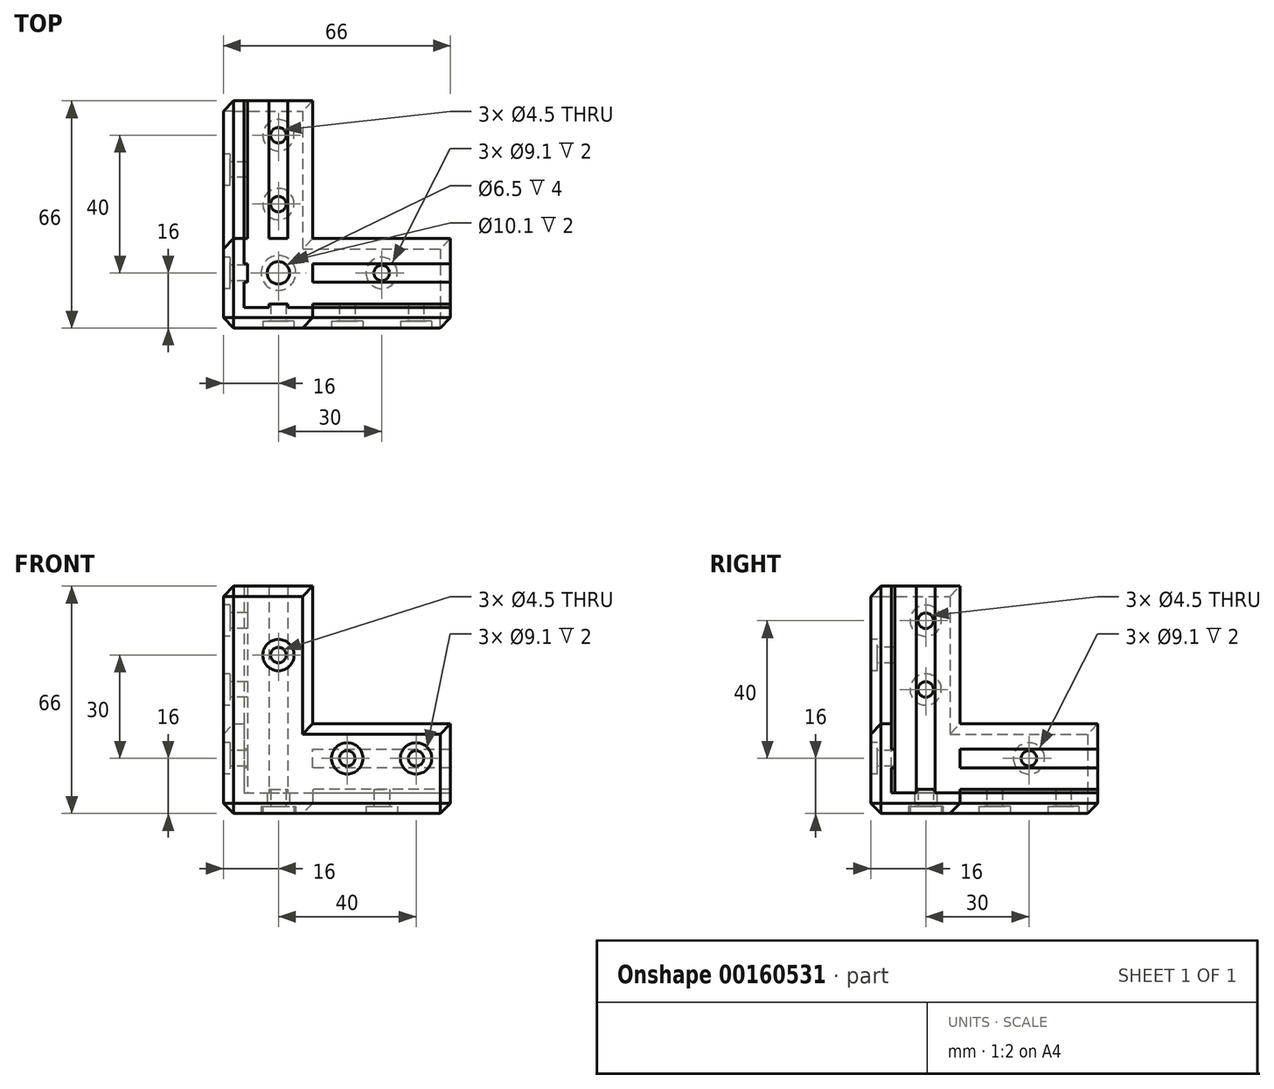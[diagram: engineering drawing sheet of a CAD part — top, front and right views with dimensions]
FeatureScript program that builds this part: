
annotation { "Feature Type Name" : "Feature", "Feature Type Description" : "" }
export const myFeature = defineFeature(function(context is Context, id is Id, definition is map)
    precondition{}
    {
        {
            var Q0;
            Q0=qCreatedBy(makeId("Top.planeOp"),FACE);
            var sketch = newSketch(context, id + "F0", { "sketchPlane" : qUnion([Q0])});
            skLineSegment(sketch, "E0", {"start": v(0, 0) * mm, "end": v(0, 66) * mm});
            skLineSegment(sketch, "E1", {"start": v(0, 66) * mm, "end": v(26, 66) * mm});
            skLineSegment(sketch, "E2", {"start": v(26, 66) * mm, "end": v(26, 26) * mm});
            skLineSegment(sketch, "E3", {"start": v(26, 26) * mm, "end": v(66, 26) * mm});
            skLineSegment(sketch, "E4", {"start": v(66, 26) * mm, "end": v(66, 0) * mm});
            skLineSegment(sketch, "E5", {"start": v(66, 0) * mm, "end": v(0, 0) * mm});
            skLineSegment(sketch, "E6", {"start": v(66, 6) * mm, "end": v(6, 6) * mm, "construction": true});
            skLineSegment(sketch, "E7", {"start": v(6, 6) * mm, "end": v(6, 66) * mm, "construction": true});
            skSolve(sketch);
        }
        {
            var Q0;
            Q0 = qSketchRegion(id + "F0", true);
            extrude(context, id + "F1", {"entities" : qUnion([Q0]), "depth" : 6 * mm});
        }
        {
            var Q0;
            Q0=makeQuery(id+"F1.opExtrude","CAP_FACE",FACE,{"disambiguationData":[OSD([sQuery(id+"F0.wireOp",EDGE,"E0"),sQuery(id+"F0.wireOp",EDGE,"E1"),sQuery(id+"F0.wireOp",EDGE,"E2"),sQuery(id+"F0.wireOp",EDGE,"E3"),sQuery(id+"F0.wireOp",EDGE,"E4"),sQuery(id+"F0.wireOp",EDGE,"E5")])],"isStart":false});
            var sketch = newSketch(context, id + "F2", { "sketchPlane" : qUnion([Q0])});
            skLineSegment(sketch, "E8", {"start": v(0, 66) * mm, "end": v(6, 66) * mm});
            skLineSegment(sketch, "E9", {"start": v(6, 66) * mm, "end": v(6, 6) * mm});
            skLineSegment(sketch, "E10", {"start": v(6, 6) * mm, "end": v(66, 6) * mm});
            skLineSegment(sketch, "E11", {"start": v(66, 6) * mm, "end": v(66, 0) * mm});
            skLineSegment(sketch, "E12", {"start": v(66, 0) * mm, "end": v(0, 0) * mm});
            skLineSegment(sketch, "E13", {"start": v(0, 0) * mm, "end": v(0, 66) * mm});
            skSolve(sketch);
        }
        {
            var Q0;
            Q0=makeQuery(id+"F2.imprint","IMPRINT",FACE,{"disambiguationData":[TD([[makeQuery(id+"F2.imprint","IMPRINT",EDGE,{"derivedFrom":sQuery(id+"F2.wireOp",EDGE,"E8")}),-1.0]])]});
            extrude(context, id + "F3", {"entities" : qUnion([Q0]), "operationType" : NewBodyOperationType.ADD, "depth" : 20 * mm});
        }
        {
            var Q0;
            Q0=makeQuery(id+"F3.opExtrude","CAP_FACE",FACE,{"disambiguationData":[OSD([sQuery(id+"F2.wireOp",EDGE,"E8"),sQuery(id+"F2.wireOp",EDGE,"E9"),sQuery(id+"F2.wireOp",EDGE,"E10"),sQuery(id+"F2.wireOp",EDGE,"E11"),sQuery(id+"F2.wireOp",EDGE,"E12"),sQuery(id+"F2.wireOp",EDGE,"E13")])],"isStart":false});
            var sketch = newSketch(context, id + "F4", { "sketchPlane" : qUnion([Q0])});
            skLineSegment(sketch, "E14", {"start": v(6, 26) * mm, "end": v(0, 26) * mm});
            skLineSegment(sketch, "E15", {"start": v(0, 26) * mm, "end": v(0, 0) * mm});
            skLineSegment(sketch, "E16", {"start": v(0, 0) * mm, "end": v(26, 0) * mm});
            skLineSegment(sketch, "E17", {"start": v(26, 0) * mm, "end": v(26, 6) * mm});
            skLineSegment(sketch, "E18", {"start": v(26, 6) * mm, "end": v(6, 6) * mm});
            skLineSegment(sketch, "E19", {"start": v(6, 6) * mm, "end": v(6, 26) * mm});
            skSolve(sketch);
        }
        {
            var Q0;
            Q0 = qSketchRegion(id + "F4", true);
            extrude(context, id + "F5", {"entities" : qUnion([Q0]), "operationType" : NewBodyOperationType.ADD, "depth" : 40 * mm});
        }
        {
            var Q0;
            Q0=makeQuery(id+"F1.opExtrude","CAP_FACE",FACE,{"disambiguationData":[OSD([sQuery(id+"F0.wireOp",EDGE,"E0"),sQuery(id+"F0.wireOp",EDGE,"E1"),sQuery(id+"F0.wireOp",EDGE,"E2"),sQuery(id+"F0.wireOp",EDGE,"E3"),sQuery(id+"F0.wireOp",EDGE,"E4"),sQuery(id+"F0.wireOp",EDGE,"E5")])],"isStart":false});
            var sketch = newSketch(context, id + "F6", { "sketchPlane" : qUnion([Q0])});
            skLineSegment(sketch, "E20", {"start": v(66, 16) * mm, "end": v(6, 16) * mm, "construction": true});
            skLineSegment(sketch, "E21", {"start": v(16, 66) * mm, "end": v(16, 6) * mm, "construction": true});
            skLineSegment(sketch, "E22", {"start": v(16, 6) * mm, "end": v(18.71, 6) * mm});
            skLineSegment(sketch, "E23", {"start": v(18.71, 6) * mm, "end": v(18.71, 7) * mm});
            skLineSegment(sketch, "E24", {"start": v(18.71, 7) * mm, "end": v(13.3, 7) * mm});
            skLineSegment(sketch, "E25", {"start": v(13.3, 7) * mm, "end": v(13.3, 6) * mm});
            skLineSegment(sketch, "E26", {"start": v(13.3, 6) * mm, "end": v(16, 6) * mm});
            skLineSegment(sketch, "E27", {"start": v(6, 16) * mm, "end": v(6, 18.7) * mm});
            skLineSegment(sketch, "E28", {"start": v(6, 18.7) * mm, "end": v(7, 18.7) * mm});
            skLineSegment(sketch, "E29", {"start": v(7, 18.7) * mm, "end": v(7, 13.29) * mm});
            skLineSegment(sketch, "E30", {"start": v(7, 13.29) * mm, "end": v(6, 13.29) * mm});
            skLineSegment(sketch, "E31", {"start": v(6, 13.29) * mm, "end": v(6, 16) * mm});
            skSolve(sketch);
        }
        {
            var Q0;
            Q0 = qSketchRegion(id + "F6", true);
            extrude(context, id + "F7", {"entities" : qUnion([Q0]), "operationType" : NewBodyOperationType.ADD, "depth" : 60 * mm});
        }
        {
            var Q0;
            Q0=makeQuery(id+"F1.opExtrude","CAP_FACE",FACE,{"disambiguationData":[OSD([sQuery(id+"F0.wireOp",EDGE,"E0"),sQuery(id+"F0.wireOp",EDGE,"E1"),sQuery(id+"F0.wireOp",EDGE,"E2"),sQuery(id+"F0.wireOp",EDGE,"E3"),sQuery(id+"F0.wireOp",EDGE,"E4"),sQuery(id+"F0.wireOp",EDGE,"E5")])],"isStart":false});
            var sketch = newSketch(context, id + "F8", { "sketchPlane" : qUnion([Q0])});
            skLineSegment(sketch, "E32", {"start": v(66, 16) * mm, "end": v(7, 16) * mm, "construction": true});
            skLineSegment(sketch, "E33", {"start": v(66, 16) * mm, "end": v(66, 18.7) * mm});
            skLineSegment(sketch, "E34", {"start": v(66, 18.7) * mm, "end": v(26, 18.7) * mm});
            skLineSegment(sketch, "E35", {"start": v(26, 18.7) * mm, "end": v(26, 13.29) * mm});
            skLineSegment(sketch, "E36", {"start": v(26, 13.29) * mm, "end": v(66, 13.29) * mm});
            skLineSegment(sketch, "E37", {"start": v(66, 13.29) * mm, "end": v(66, 16) * mm});
            skLineSegment(sketch, "E38", {"start": v(16, 66) * mm, "end": v(16, 7) * mm, "construction": true});
            skLineSegment(sketch, "E39", {"start": v(16, 66) * mm, "end": v(13.3, 66) * mm});
            skLineSegment(sketch, "E40", {"start": v(13.3, 66) * mm, "end": v(13.3, 26) * mm});
            skLineSegment(sketch, "E41", {"start": v(13.3, 26) * mm, "end": v(18.7, 26) * mm});
            skLineSegment(sketch, "E42", {"start": v(18.7, 26) * mm, "end": v(18.7, 66) * mm});
            skLineSegment(sketch, "E43", {"start": v(18.7, 66) * mm, "end": v(16, 66) * mm});
            skSolve(sketch);
        }
        {
            var Q0;
            Q0 = qSketchRegion(id + "F8", true);
            extrude(context, id + "F9", {"entities" : qUnion([Q0]), "operationType" : NewBodyOperationType.ADD, "flatOperationType" : FlatOperationType.REMOVE, "offsetDistance" : 25 * mm, "depth" : 1 * mm, "domain" : OperationDomain.MODEL});
        }
        {
            var Q0;
            {var subQ1=sQuery(id+"F2.wireOp",EDGE,"E10");var subQ2=sQuery(id+"F0.wireOp",EDGE,"E4");var subQ3=sQuery(id+"F4.wireOp",EDGE,"E18");Q0=makeQuery(id+"F7.boolean.opBoolean","SPLIT",FACE,{"disambiguationData":[TD([makeQuery(id+"F1.opExtrude","SWEPT_FACE",FACE,{"disambiguationData":[OSD([subQ2])]})])],"derivedFrom":makeQuery(id+"F5.boolean.opBoolean","MERGE",FACE,{"derivedFrom":[makeQuery(id+"F3.opExtrude","SWEPT_FACE",FACE,{"disambiguationData":[OSD([subQ1])]}),makeQuery(id+"F5.opExtrude","SWEPT_FACE",FACE,{"disambiguationData":[OSD([subQ3])]})]})});}
            var sketch = newSketch(context, id + "F10", { "sketchPlane" : qUnion([Q0])});
            skLineSegment(sketch, "E44", {"start": v(-66, 16) * mm, "end": v(-26, 16) * mm, "construction": true});
            skLineSegment(sketch, "E45", {"start": v(-66, 16) * mm, "end": v(-66, 13.3) * mm});
            skLineSegment(sketch, "E46", {"start": v(-66, 13.3) * mm, "end": v(-26, 13.3) * mm});
            skLineSegment(sketch, "E47", {"start": v(-26, 13.3) * mm, "end": v(-26, 16) * mm});
            skLineSegment(sketch, "E48", {"start": v(-26, 18.71) * mm, "end": v(-66, 18.71) * mm});
            skLineSegment(sketch, "E49", {"start": v(-66, 18.71) * mm, "end": v(-66, 16) * mm});
            skLineSegment(sketch, "E50", {"start": v(-26, 18.71) * mm, "end": v(-26, 16) * mm});
            skSolve(sketch);
        }
        {
            var Q0;
            Q0 = qSketchRegion(id + "F10", true);
            extrude(context, id + "F11", {"entities" : qUnion([Q0]), "operationType" : NewBodyOperationType.ADD, "flatOperationType" : FlatOperationType.REMOVE, "offsetDistance" : 25 * mm, "depth" : 1 * mm, "domain" : OperationDomain.MODEL});
        }
        {
            var Q0;
            {var subQ0=sQuery(id+"F2.wireOp",EDGE,"E9");var subQ3=sQuery(id+"F0.wireOp",EDGE,"E1");var subQ5=sQuery(id+"F4.wireOp",EDGE,"E19");Q0=makeQuery(id+"F7.boolean.opBoolean","SPLIT",FACE,{"disambiguationData":[TD([makeQuery(id+"F1.opExtrude","SWEPT_FACE",FACE,{"disambiguationData":[OSD([subQ3])]})])],"derivedFrom":makeQuery(id+"F5.boolean.opBoolean","MERGE",FACE,{"derivedFrom":[makeQuery(id+"F3.opExtrude","SWEPT_FACE",FACE,{"disambiguationData":[OSD([subQ0])]}),makeQuery(id+"F5.opExtrude","SWEPT_FACE",FACE,{"disambiguationData":[OSD([subQ5])]})]})});}
            var sketch = newSketch(context, id + "F12", { "sketchPlane" : qUnion([Q0])});
            skLineSegment(sketch, "E51", {"start": v(66, 16) * mm, "end": v(26, 16) * mm, "construction": true});
            skLineSegment(sketch, "E52", {"start": v(66, 16) * mm, "end": v(66, 18.71) * mm});
            skLineSegment(sketch, "E53", {"start": v(66, 18.71) * mm, "end": v(26, 18.7) * mm});
            skLineSegment(sketch, "E54", {"start": v(26, 18.7) * mm, "end": v(26, 13.29) * mm});
            skLineSegment(sketch, "E55", {"start": v(26, 13.29) * mm, "end": v(66, 13.29) * mm});
            skLineSegment(sketch, "E56", {"start": v(66, 16) * mm, "end": v(66, 13.29) * mm});
            skSolve(sketch);
        }
        {
            var Q0;
            Q0 = qSketchRegion(id + "F12", true);
            extrude(context, id + "F13", {"entities" : qUnion([Q0]), "operationType" : NewBodyOperationType.ADD, "flatOperationType" : FlatOperationType.REMOVE, "offsetDistance" : 25 * mm, "depth" : 1 * mm, "domain" : OperationDomain.MODEL});
        }
        {
            var Q0;
            Q0=makeQuery(id+"F5.boolean.opBoolean","MERGE",FACE,{"derivedFrom":[makeQuery(id+"F3.boolean.opBoolean","MERGE",FACE,{"derivedFrom":[makeQuery(id+"F1.opExtrude","SWEPT_FACE",FACE,{"disambiguationData":[OSD([sQuery(id+"F0.wireOp",EDGE,"E5")])]}),makeQuery(id+"F3.opExtrude","SWEPT_FACE",FACE,{"disambiguationData":[OSD([sQuery(id+"F2.wireOp",EDGE,"E12")])]})]}),makeQuery(id+"F5.opExtrude","SWEPT_FACE",FACE,{"disambiguationData":[OSD([sQuery(id+"F4.wireOp",EDGE,"E16")])]})]});
            var sketch = newSketch(context, id + "F14", { "sketchPlane" : qUnion([Q0])});
            skLineSegment(sketch, "E57", {"start": v(6, 66) * mm, "end": v(6, 6) * mm, "construction": true});
            skLineSegment(sketch, "E58", {"start": v(6, 6) * mm, "end": v(66, 6) * mm, "construction": true});
            skCircle(sketch, "E59", {"center": v(56, 16) * mm, "radius": 2.25 * mm});
            skCircle(sketch, "E60", {"center": v(36, 16) * mm, "radius": 2.25 * mm});
            skCircle(sketch, "E61", {"center": v(16, 46) * mm, "radius": 2.25 * mm});
            skLineSegment(sketch, "E62", {"start": v(26, 26) * mm, "end": v(6, 26) * mm, "construction": true});
            skLineSegment(sketch, "E63", {"start": v(26, 26) * mm, "end": v(26, 6) * mm, "construction": true});
            skSolve(sketch);
        }
        {
            var Q0;
            Q0=makeQuery(id+"F14.imprint","IMPRINT",FACE,{"disambiguationData":[TD([[makeQuery(id+"F14.imprint","IMPRINT",EDGE,{"derivedFrom":sQuery(id+"F14.wireOp",EDGE,"E59")}),1.0]])]});
            var Q1;
            Q1=makeQuery(id+"F14.imprint","IMPRINT",FACE,{"disambiguationData":[TD([[makeQuery(id+"F14.imprint","IMPRINT",EDGE,{"derivedFrom":sQuery(id+"F14.wireOp",EDGE,"E61")}),1.0]])]});
            var Q2;
            Q2=makeQuery(id+"F14.imprint","IMPRINT",FACE,{"disambiguationData":[TD([[makeQuery(id+"F14.imprint","IMPRINT",EDGE,{"derivedFrom":sQuery(id+"F14.wireOp",EDGE,"E60")}),1.0]])]});
            extrude(context, id + "F15", {"entities" : qUnion([Q0, Q1, Q2]), "operationType" : NewBodyOperationType.REMOVE, "endBound" : BoundingType.UP_TO_NEXT, "oppositeDirection" : true, "depth" : 25 * mm});
        }
        {
            var Q0;
            Q0=makeQuery(id+"F5.boolean.opBoolean","MERGE",FACE,{"derivedFrom":[makeQuery(id+"F3.boolean.opBoolean","MERGE",FACE,{"derivedFrom":[makeQuery(id+"F1.opExtrude","SWEPT_FACE",FACE,{"disambiguationData":[OSD([sQuery(id+"F0.wireOp",EDGE,"E0")])]}),makeQuery(id+"F3.opExtrude","SWEPT_FACE",FACE,{"disambiguationData":[OSD([sQuery(id+"F2.wireOp",EDGE,"E13")])]})]}),makeQuery(id+"F5.opExtrude","SWEPT_FACE",FACE,{"disambiguationData":[OSD([sQuery(id+"F4.wireOp",EDGE,"E15")])]})]});
            var sketch = newSketch(context, id + "F16", { "sketchPlane" : qUnion([Q0])});
            skLineSegment(sketch, "E64", {"start": v(-6, 66) * mm, "end": v(-6, 6) * mm, "construction": true});
            skLineSegment(sketch, "E65", {"start": v(-6, 6) * mm, "end": v(-66, 6) * mm, "construction": true});
            skCircle(sketch, "E66", {"center": v(-16, 56) * mm, "radius": 2.25 * mm});
            skCircle(sketch, "E67", {"center": v(-46, 16) * mm, "radius": 2.25 * mm});
            skCircle(sketch, "E68", {"center": v(-16, 36) * mm, "radius": 2.25 * mm});
            skSolve(sketch);
        }
        {
            var Q0;
            Q0 = qSketchRegion(id + "F16", true);
            extrude(context, id + "F17", {"entities" : qUnion([Q0]), "operationType" : NewBodyOperationType.REMOVE, "endBound" : BoundingType.UP_TO_NEXT, "oppositeDirection" : true, "depth" : 25 * mm});
        }
        {
            var Q0;
            Q0=makeQuery(id+"F1.opExtrude","CAP_FACE",FACE,{"disambiguationData":[OSD([sQuery(id+"F0.wireOp",EDGE,"E0"),sQuery(id+"F0.wireOp",EDGE,"E1"),sQuery(id+"F0.wireOp",EDGE,"E2"),sQuery(id+"F0.wireOp",EDGE,"E3"),sQuery(id+"F0.wireOp",EDGE,"E4"),sQuery(id+"F0.wireOp",EDGE,"E5")])],"isStart":true});
            var sketch = newSketch(context, id + "F18", { "sketchPlane" : qUnion([Q0])});
            skLineSegment(sketch, "E69", {"start": v(66, -6) * mm, "end": v(6, -6) * mm, "construction": true});
            skLineSegment(sketch, "E70", {"start": v(6, -6) * mm, "end": v(6, -66) * mm, "construction": true});
            skCircle(sketch, "E71", {"center": v(16, -16) * mm, "radius": 3.25 * mm});
            skCircle(sketch, "E72", {"center": v(46, -16) * mm, "radius": 2.25 * mm});
            skCircle(sketch, "E73", {"center": v(16, -56) * mm, "radius": 2.25 * mm});
            skCircle(sketch, "E74", {"center": v(16, -36) * mm, "radius": 2.25 * mm});
            skSolve(sketch);
        }
        {
            var Q0;
            Q0 = qSketchRegion(id + "F18", true);
            extrude(context, id + "F19", {"entities" : qUnion([Q0]), "operationType" : NewBodyOperationType.REMOVE, "endBound" : BoundingType.UP_TO_NEXT, "oppositeDirection" : true, "depth" : 25 * mm});
        }
        {
            var Q0;
            Q0=makeQuery(id+"F5.boolean.opBoolean","MERGE",FACE,{"derivedFrom":[makeQuery(id+"F3.boolean.opBoolean","MERGE",FACE,{"derivedFrom":[makeQuery(id+"F1.opExtrude","SWEPT_FACE",FACE,{"disambiguationData":[OSD([sQuery(id+"F0.wireOp",EDGE,"E5")])]}),makeQuery(id+"F3.opExtrude","SWEPT_FACE",FACE,{"disambiguationData":[OSD([sQuery(id+"F2.wireOp",EDGE,"E12")])]})]}),makeQuery(id+"F5.opExtrude","SWEPT_FACE",FACE,{"disambiguationData":[OSD([sQuery(id+"F4.wireOp",EDGE,"E16")])]})]});
            var sketch = newSketch(context, id + "F20", { "sketchPlane" : qUnion([Q0])});
            skCircle(sketch, "E75", {"center": v(16, 46) * mm, "radius": 4.55 * mm});
            skCircle(sketch, "E76", {"center": v(36, 16) * mm, "radius": 4.55 * mm});
            skCircle(sketch, "E77", {"center": v(56, 16) * mm, "radius": 4.55 * mm});
            skSolve(sketch);
        }
        {
            var Q0;
            Q0 = qSketchRegion(id + "F20", true);
            extrude(context, id + "F21", {"entities" : qUnion([Q0]), "operationType" : NewBodyOperationType.REMOVE, "oppositeDirection" : true, "depth" : 2 * mm});
        }
        {
            var Q0;
            Q0=makeQuery(id+"F5.boolean.opBoolean","MERGE",FACE,{"derivedFrom":[makeQuery(id+"F3.boolean.opBoolean","MERGE",FACE,{"derivedFrom":[makeQuery(id+"F1.opExtrude","SWEPT_FACE",FACE,{"disambiguationData":[OSD([sQuery(id+"F0.wireOp",EDGE,"E0")])]}),makeQuery(id+"F3.opExtrude","SWEPT_FACE",FACE,{"disambiguationData":[OSD([sQuery(id+"F2.wireOp",EDGE,"E13")])]})]}),makeQuery(id+"F5.opExtrude","SWEPT_FACE",FACE,{"disambiguationData":[OSD([sQuery(id+"F4.wireOp",EDGE,"E15")])]})]});
            var sketch = newSketch(context, id + "F22", { "sketchPlane" : qUnion([Q0])});
            skCircle(sketch, "E78", {"center": v(-16, 56) * mm, "radius": 4.55 * mm});
            skCircle(sketch, "E79", {"center": v(-46, 16) * mm, "radius": 4.55 * mm});
            skCircle(sketch, "E80", {"center": v(-16, 36) * mm, "radius": 4.55 * mm});
            skSolve(sketch);
        }
        {
            var Q0;
            Q0 = qSketchRegion(id + "F22", true);
            extrude(context, id + "F23", {"entities" : qUnion([Q0]), "operationType" : NewBodyOperationType.REMOVE, "oppositeDirection" : true, "depth" : 2 * mm});
        }
        {
            var Q0;
            Q0=makeQuery(id+"F1.opExtrude","CAP_FACE",FACE,{"disambiguationData":[OSD([sQuery(id+"F0.wireOp",EDGE,"E0"),sQuery(id+"F0.wireOp",EDGE,"E1"),sQuery(id+"F0.wireOp",EDGE,"E2"),sQuery(id+"F0.wireOp",EDGE,"E3"),sQuery(id+"F0.wireOp",EDGE,"E4"),sQuery(id+"F0.wireOp",EDGE,"E5")])],"isStart":true});
            var sketch = newSketch(context, id + "F24", { "sketchPlane" : qUnion([Q0])});
            skCircle(sketch, "E81", {"center": v(16, -56) * mm, "radius": 4.55 * mm});
            skCircle(sketch, "E82", {"center": v(16, -16) * mm, "radius": 5.05 * mm});
            skCircle(sketch, "E83", {"center": v(46, -16) * mm, "radius": 4.55 * mm});
            skCircle(sketch, "E84", {"center": v(16, -36) * mm, "radius": 4.55 * mm});
            skSolve(sketch);
        }
        {
            var Q0;
            Q0 = qSketchRegion(id + "F24", true);
            extrude(context, id + "F25", {"entities" : qUnion([Q0]), "operationType" : NewBodyOperationType.REMOVE, "oppositeDirection" : true, "depth" : 2 * mm});
        }
        {
            var Q0;
            Q0=makeQuery(id+"F1.opExtrude","CAP_EDGE",EDGE,{"disambiguationData":[OSD([sQuery(id+"F0.wireOp",EDGE,"E5")])],"isStart":true});
            var Q1;
            Q1=makeQuery(id+"F1.opExtrude","CAP_EDGE",EDGE,{"disambiguationData":[OSD([sQuery(id+"F0.wireOp",EDGE,"E0")])],"isStart":true});
            var Q2;
            Q2=makeQuery(id+"F5.boolean.opBoolean","MERGE",EDGE,{"derivedFrom":[makeQuery(id+"F3.boolean.opBoolean","MERGE",EDGE,{"derivedFrom":[makeQuery(id+"F1.opExtrude","SWEPT_EDGE",EDGE,{"disambiguationData":[OSD([sQuery(id+"F0.wireOp",EDGE,"E0"),sQuery(id+"F0.wireOp",EDGE,"E5")])]}),makeQuery(id+"F3.opExtrude","SWEPT_EDGE",EDGE,{"disambiguationData":[OSD([sQuery(id+"F2.wireOp",EDGE,"E12"),sQuery(id+"F2.wireOp",EDGE,"E13")])]})]}),makeQuery(id+"F5.opExtrude","SWEPT_EDGE",EDGE,{"disambiguationData":[OSD([sQuery(id+"F4.wireOp",EDGE,"E15"),sQuery(id+"F4.wireOp",EDGE,"E16")])]})]});
            var Q3;
            Q3=makeQuery(id+"F5.opExtrude","SWEPT_EDGE",EDGE,{"disambiguationData":[OSD([sQuery(id+"F2.wireOp",EDGE,"E13"),sQuery(id+"F4.wireOp",EDGE,"E14"),sQuery(id+"F4.wireOp",EDGE,"E15")])]});
            var Q4;
            Q4=makeQuery(id+"F3.opExtrude","CAP_EDGE",EDGE,{"disambiguationData":[OSD([sQuery(id+"F2.wireOp",EDGE,"E13")])],"isStart":false});
            var Q5;
            Q5=makeQuery(id+"F5.opExtrude","SWEPT_EDGE",EDGE,{"disambiguationData":[OSD([sQuery(id+"F2.wireOp",EDGE,"E12"),sQuery(id+"F4.wireOp",EDGE,"E16"),sQuery(id+"F4.wireOp",EDGE,"E17")])]});
            var Q6;
            Q6=makeQuery(id+"F3.opExtrude","CAP_EDGE",EDGE,{"disambiguationData":[OSD([sQuery(id+"F2.wireOp",EDGE,"E12")])],"isStart":false});
            var Q7;
            Q7=makeQuery(id+"F5.opExtrude","CAP_EDGE",EDGE,{"disambiguationData":[OSD([sQuery(id+"F4.wireOp",EDGE,"E15")])],"isStart":false});
            var Q8;
            Q8=makeQuery(id+"F5.opExtrude","CAP_EDGE",EDGE,{"disambiguationData":[OSD([sQuery(id+"F4.wireOp",EDGE,"E16")])],"isStart":false});
            var Q9;
            Q9=makeQuery(id+"F3.boolean.opBoolean","MERGE",EDGE,{"derivedFrom":[makeQuery(id+"F1.opExtrude","SWEPT_EDGE",EDGE,{"disambiguationData":[OSD([sQuery(id+"F0.wireOp",EDGE,"E0"),sQuery(id+"F0.wireOp",EDGE,"E1")])]}),makeQuery(id+"F3.opExtrude","SWEPT_EDGE",EDGE,{"disambiguationData":[OSD([sQuery(id+"F2.wireOp",EDGE,"E8"),sQuery(id+"F2.wireOp",EDGE,"E13")])]})]});
            var Q10;
            Q10=makeQuery(id+"F1.opExtrude","CAP_EDGE",EDGE,{"disambiguationData":[OSD([sQuery(id+"F0.wireOp",EDGE,"E1")])],"isStart":true});
            var Q11;
            Q11=makeQuery(id+"F3.boolean.opBoolean","MERGE",EDGE,{"derivedFrom":[makeQuery(id+"F1.opExtrude","SWEPT_EDGE",EDGE,{"disambiguationData":[OSD([sQuery(id+"F0.wireOp",EDGE,"E4"),sQuery(id+"F0.wireOp",EDGE,"E5")])]}),makeQuery(id+"F3.opExtrude","SWEPT_EDGE",EDGE,{"disambiguationData":[OSD([sQuery(id+"F2.wireOp",EDGE,"E11"),sQuery(id+"F2.wireOp",EDGE,"E12")])]})]});
            var Q12;
            Q12=makeQuery(id+"F1.opExtrude","CAP_EDGE",EDGE,{"disambiguationData":[OSD([sQuery(id+"F0.wireOp",EDGE,"E4")])],"isStart":true});
            var Q13;
            Q13=makeQuery(id+"F1.opExtrude","CAP_EDGE",EDGE,{"disambiguationData":[OSD([sQuery(id+"F0.wireOp",EDGE,"E3")])],"isStart":true});
            var Q14;
            Q14=makeQuery(id+"F1.opExtrude","CAP_EDGE",EDGE,{"disambiguationData":[OSD([sQuery(id+"F0.wireOp",EDGE,"E2")])],"isStart":true});
            chamfer(context, id + "F26", {"entities" : qUnion([Q0, Q1, Q2, Q3, Q4, Q5, Q6, Q7, Q8, Q9, Q10, Q11, Q12, Q13, Q14]), "width" : 3 * mm, "tangentPropagation" : true});
        }
    });
